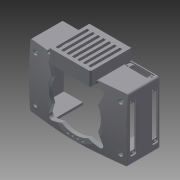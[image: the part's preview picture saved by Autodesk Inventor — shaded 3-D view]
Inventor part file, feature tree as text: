
AUTODESK INVENTOR PART (.ipt)
format: ipt  version: 2013 (Build 170138000, 138)  size: 1,346,048 bytes
history: native  units: in
note: dims shown in document units (in); Inventor stores cm internally (conversion verified against a paired STEP export)
features: extrude x27, sketch x27, fillet x12, projected_geometry x8, reference x5, plane x4
ambient origin geometry x8: Origin, YZ Plane, XZ Plane, XY Plane, X Axis, Y Axis, Z Axis, Center Point
bodies: Solid1 (feature_tree)
feature tree (83):
  extrude  "Extrusion1"  Depth=1.2598in TaperAngle=0.0deg
  extrude  "Extrusion3"  Depth=2.2047in
  extrude  "Extrusion21"  Depth=3.937in TaperAngle=0.0deg
  extrude  "Extrusion2"  TaperAngle=0.0deg  [1 undecoded]
  plane  "Work Plane1"
  extrude  "Extrusion23"  Depth=0.0394in
  extrude  "Extrusion4"  Depth=2.25in
  extrude  "Extrusion5"  Depth=0.15in
  fillet  "Fillet9"  Radius=0.0984in
  fillet  "Fillet15"  Radius=0.0984in
  extrude  "Extrusion20"  Depth=2.2047in
  plane  "Work Plane2"
  extrude  "Extrusion6"  Depth=0.0787in
  extrude  "Extrusion24"  Depth=0.0394in
  fillet  "Fillet11"  Radius=0.0394in
  plane  "Work Plane3"
  extrude  "Extrusion26"  Depth=0.6496in
  sketch  "Sketch39"  dims[d69=0.1575in d78=0.6496in]
  plane  "Work Plane4"
  extrude  "Extrusion30"  Depth=0.2854in
  extrude  "Extrusion31"  Depth=0.0787in
  sketch  "Sketch42"  dims[d186=2.2047in d187=1.9685in d188=0.5497in]
  extrude  "Extrusion32"  Depth=1.9685in
  extrude  "Extrusion33"  [1 undecoded]
  extrude  "Extrusion34"  Depth=1.9509in
  extrude  "Extrusion35"  Depth=4.2362in
  fillet  "Fillet12"  Radius=0.1307in
  fillet  "Fillet13"  Radius=2.4409in
  extrude  "Extrusion36"  [1 undecoded]
  fillet  "Fillet14"  Radius=0.1969in
  extrude  "Extrusion37"  Depth=0.0236in
  extrude  "Extrusion27"  Depth=1.2598in TaperAngle=0.0deg
  extrude  "Extrusion38"  Depth=1.378in
  extrude  "Extrusion39"  Depth=2.7559in
  extrude  "Extrusion40"  Depth=2.3756in
  fillet  "Fillet16"  Radius=2.3622in
  extrude  "Extrusion41"  Depth=0.3937in TaperAngle=0.0deg
  extrude  "Extrusion42"  Depth=0.1378in
  extrude  "Extrusion43"  Depth=0.1378in
  extrude  "Extrusion44"  Depth=1.7717in
  fillet  "Fillet17"  Radius=0.2756in
  fillet  "Fillet18"  Radius=0.4724in
  fillet  "Fillet19"  Radius=0.2756in
  fillet  "Fillet20"  Radius=0.0787in
  fillet  "Fillet21"  Radius=1.9685in
  sketch  "Sketch4"  dims[d6=0.4331in d7=0.0in d9=1.2598in d10=0.0in]
  reference  "Reference2"
  reference  "Reference3"
  reference  "Reference4"
  reference  "Reference5"
  sketch  "Sketch5"  dims[d12=0.3937in d13=0.0in d28=2.2047in]
  projected_geometry  "Projected Loop1"
  reference  "Reference14"
  sketch  "Sketch6"  dims[d29=2.2047in d31=3.937in d32=0.0in]
  sketch  "Sketch7"  dims[d41=0.2756in d42=0.0in]
  sketch  "Sketch24"  dims[d44=0.1181in d45=0.0394in]
  sketch  "Sketch25"  dims[d46=0.0394in d47=2.25in]
  sketch  "Sketch28"  dims[d49=4.0in d50=0.15in d51=0.0984in d52=0.0984in]
  sketch  "Sketch31"  dims[d54=0.0984in d59=2.2047in]
  projected_geometry  "Projected Loop8"
  sketch  "Sketch33"  dims[d62=0.0984in d63=0.0in d64=0.0787in]
  projected_geometry  "Projected Loop10"
  sketch  "Sketch34"  dims[d66=0.1181in d67=0.0394in d68=0.0394in]
  sketch  "Sketch40"  dims[d79=0.2854in d80=0.2854in]
  sketch  "Sketch41"  dims[d81=0.1969in d82=0.0in d184=0.0787in]
  sketch  "Sketch43"  dims[d189=1.9685in d190=0.5635in d191=-0.2756in]
  sketch  "Sketch44"  dims[d196=2.4409in d198=1.9509in]
  sketch  "Sketch45"  dims[d199=2.7165in d202=4.2362in d203=0.1307in d209=2.4409in]
  sketch  "Sketch46"  dims[d210=1.9685in d211=0.536in d213=-0.1969in d214=0.1969in]
  sketch  "Sketch47"  dims[d215=0.2362in d216=0.0in d217=0.0236in]
  sketch  "Sketch48"  dims[d218=0.1181in d224=1.2598in d225=0.0in]
  projected_geometry  "Projected Loop13"
  sketch  "Sketch49"  dims[d226=0.1181in d228=1.378in]
  projected_geometry  "Projected Loop14"
  sketch  "Sketch50"  dims[d229=0.0394in d232=2.7559in d234=0.2362in d235=0.3937in d237=0.3937in]
  sketch  "Sketch51"  dims[d239=0.5118in d240=0.0in d270=2.3756in d272=2.3622in]
  sketch  "Sketch52"  dims[d273=0.315in d274=0.3937in d275=0.0in]
  sketch  "Sketch53"  dims[d278=0.0984in d279=0.0in d280=0.1378in]
  sketch  "Sketch54"  dims[d281=0.1378in d282=0.1378in]
  sketch  "Sketch55"  dims[d308=0.3937in d309=0.0in d310=1.7717in d312=0.2756in d313=0.4724in d314=0.2756in d315=0.0787in d316=1.9685in d317=0.0in d330=0.0in d331=0.1575in d332=0.1575in d333=0.0in d334=0.0787in d335=0.0591in d336=0.0in d337=0.0787in d340=0.0in d341=0.0787in d342=0.0in d343=0.0079in d344=0.0079in d345=0.1102in d346=0.2756in d347=1.5748in d348=1.1002in d349=2.1in d350=1.95in d351=0.1102in d352=0.1102in d353=1.0651in d354=1.0651in d355=1.2179in d356=1.122in d357=1.0651in d358=0.1378in d359=1.0651in d360=1.122in d368=0.2362in d369=0.0in d370=0.1969in d371=0.0in d372=0.1181in d373=0.0787in d374=0.1475in d375=0.88in d377=0.4724in d378=0.0984in d379=0.3937in d380=0.315in d381=0.0in d382=0.0in d384=0.0in d385=1.811in d386=1.2126in d387=1.2126in d388=0.0787in d389=0.0in d390=0.1378in d391=0.1378in d392=1.6142in d394=0.0787in d395=0.1181in d396=0.0in d397=0.0787in d398=0.0in d399=0.0394in d400=1.7717in d401=0.2756in d402=0.0787in d403=0.6693in d404=0.5118in d405=0.1969in d406=0.0in d411=0.0787in d412=0.1575in d413=0.1575in d414=0.0in d415=0.0in d416=0.0591in d417=0.0in d418=0.0079in d419=0.0787in d420=0.0787in d421=0.0787in d422=0.0in d423=0.2756in d425=0.0787in d426=0.7874in d427=0.0394in d428=0.2756in d429=0.3937in d430=0.0in d431=0.0787in d432=0.1575in d433=0.1575in d434=0.0591in d435=0.0in d436=0.0787in d437=0.0787in d438=0.0787in d439=0.0in d441=0.5906in d442=0.0787in d443=0.0787in d444=0.0079in d445=0.0079in d446=0.0079in]
  projected_geometry  "Projected Loop15"
  projected_geometry  "Projected Loop16"
  projected_geometry  "Projected Loop17"
note: 3 required parameter values undecoded (feature->parameter linkage not recoverable at this tier; creation-order binding heuristic only, values carry confidence <= 0.55)
